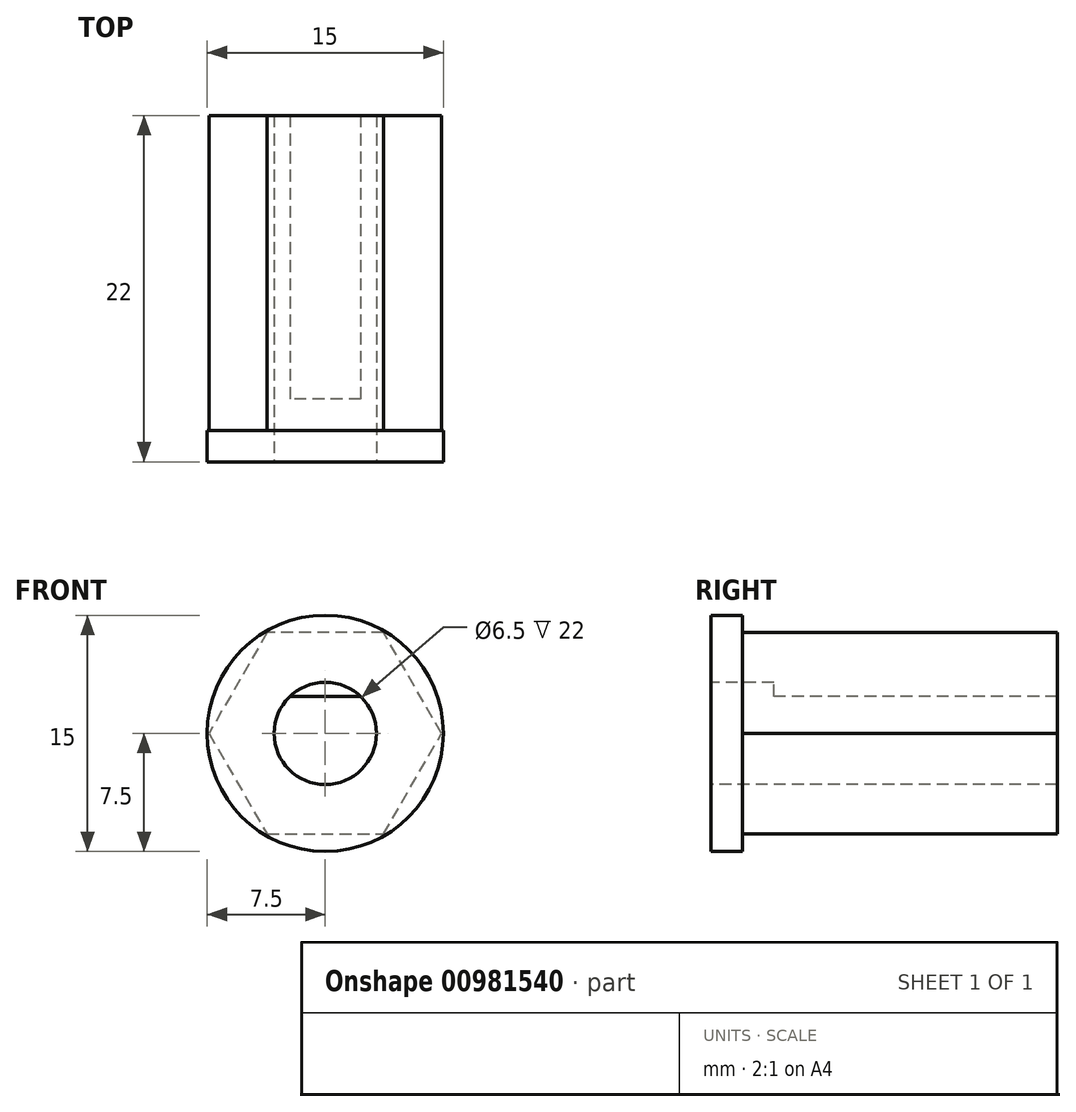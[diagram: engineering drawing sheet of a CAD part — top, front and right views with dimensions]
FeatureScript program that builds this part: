
annotation { "Feature Type Name" : "Feature", "Feature Type Description" : "" }
export const myFeature = defineFeature(function(context is Context, id is Id, definition is map)
    precondition{}
    {
        {
            var Q0;
            Q0=qCreatedBy(makeId("Front.planeOp"),FACE);
            var sketch = newSketch(context, id + "F0", { "sketchPlane" : qUnion([Q0])});
            skCircle(sketch, "E0", {"center": v(0, 0) * mm, "radius": 7.5 * mm});
            skSolve(sketch);
        }
        {
            var Q0;
            Q0 = qSketchRegion(id + "F0", true);
            extrude(context, id + "F1", {"entities" : qUnion([Q0]), "oppositeDirection" : true, "depth" : 22 * mm, "offsetDistance" : 25 * mm});
        }
        {
            var Q0;
            Q0=makeQuery(id+"F1.opExtrude","CAP_FACE",FACE,{"disambiguationData":[OSD([sQuery(id+"F0.wireOp",EDGE,"E0")])],"isStart":false});
            var sketch = newSketch(context, id + "F2", { "sketchPlane" : qUnion([Q0])});
            skCircle(sketch, "E1.cCircle", {"center": v(0, 0) * mm, "radius": 7.4 * mm, "construction": true});
            skLineSegment(sketch, "E1.0", {"start": v(7.4, 0) * mm, "end": v(3.7, -6.4) * mm});
            skLineSegment(sketch, "E1.1", {"start": v(3.7, -6.4) * mm, "end": v(-3.7, -6.4) * mm});
            skLineSegment(sketch, "E1.2", {"start": v(-3.7, -6.4) * mm, "end": v(-7.4, 0) * mm});
            skLineSegment(sketch, "E1.3", {"start": v(-7.4, 0) * mm, "end": v(-3.7, 6.4) * mm});
            skLineSegment(sketch, "E1.4", {"start": v(-3.7, 6.4) * mm, "end": v(3.7, 6.4) * mm});
            skLineSegment(sketch, "E1.5", {"start": v(3.7, 6.4) * mm, "end": v(7.4, 0) * mm});
            skCircle(sketch, "E2", {"center": v(0, 0) * mm, "radius": 8 * mm});
            skSolve(sketch);
        }
        {
            var Q0;
            Q0 = qSketchRegion(id + "F2", true);
            extrude(context, id + "F3", {"entities" : qUnion([Q0]), "operationType" : NewBodyOperationType.REMOVE, "oppositeDirection" : true, "depth" : 20 * mm, "offsetDistance" : 25 * mm});
        }
        {
            var Q0;
            Q0=makeQuery(id+"F1.opExtrude","CAP_FACE",FACE,{"disambiguationData":[OSD([sQuery(id+"F0.wireOp",EDGE,"E0")])],"isStart":true});
            var sketch = newSketch(context, id + "F4", { "sketchPlane" : qUnion([Q0])});
            skCircle(sketch, "E3", {"center": v(0, 0) * mm, "radius": 3.25 * mm, "construction": true});
            skLineSegment(sketch, "E4", {"start": v(0, -3.25) * mm, "end": v(0, 2.35) * mm, "construction": true});
            skLineSegment(sketch, "E5", {"start": v(0, 2.35) * mm, "end": v(2.24, 2.35) * mm, "construction": true});
            skLineSegment(sketch, "E6", {"start": v(2.24, 2.35) * mm, "end": v(-2.24, 2.35) * mm, "construction": true});
            skArc(sketch, "E7", {"start": v(-2.24, 2.35) * mm, "mid": v(0, -3.25) * mm, "end": v(2.24, 2.35) * mm});
            skLineSegment(sketch, "E8", {"start": v(-2.24, 2.35) * mm, "end": v(2.24, 2.35) * mm});
            skSolve(sketch);
        }
        {
            var Q0;
            Q0 = qSketchRegion(id + "F4", true);
            extrude(context, id + "F5", {"entities" : qUnion([Q0]), "operationType" : NewBodyOperationType.REMOVE, "endBound" : BoundingType.THROUGH_ALL, "oppositeDirection" : true, "depth" : 15 * mm, "offsetDistance" : 25 * mm});
        }
        {
            var Q0;
            Q0=makeQuery(id+"F1.opExtrude","CAP_FACE",FACE,{"disambiguationData":[OSD([sQuery(id+"F0.wireOp",EDGE,"E0")])],"isStart":true});
            var sketch = newSketch(context, id + "F6", { "sketchPlane" : qUnion([Q0])});
            skCircle(sketch, "E9", {"center": v(0, 0) * mm, "radius": 3.25 * mm});
            skSolve(sketch);
        }
        {
            var Q0;
            Q0 = qSketchRegion(id + "F6", true);
            extrude(context, id + "F7", {"entities" : qUnion([Q0]), "operationType" : NewBodyOperationType.REMOVE, "oppositeDirection" : true, "depth" : 4 * mm, "offsetDistance" : 25 * mm});
        }
    });
